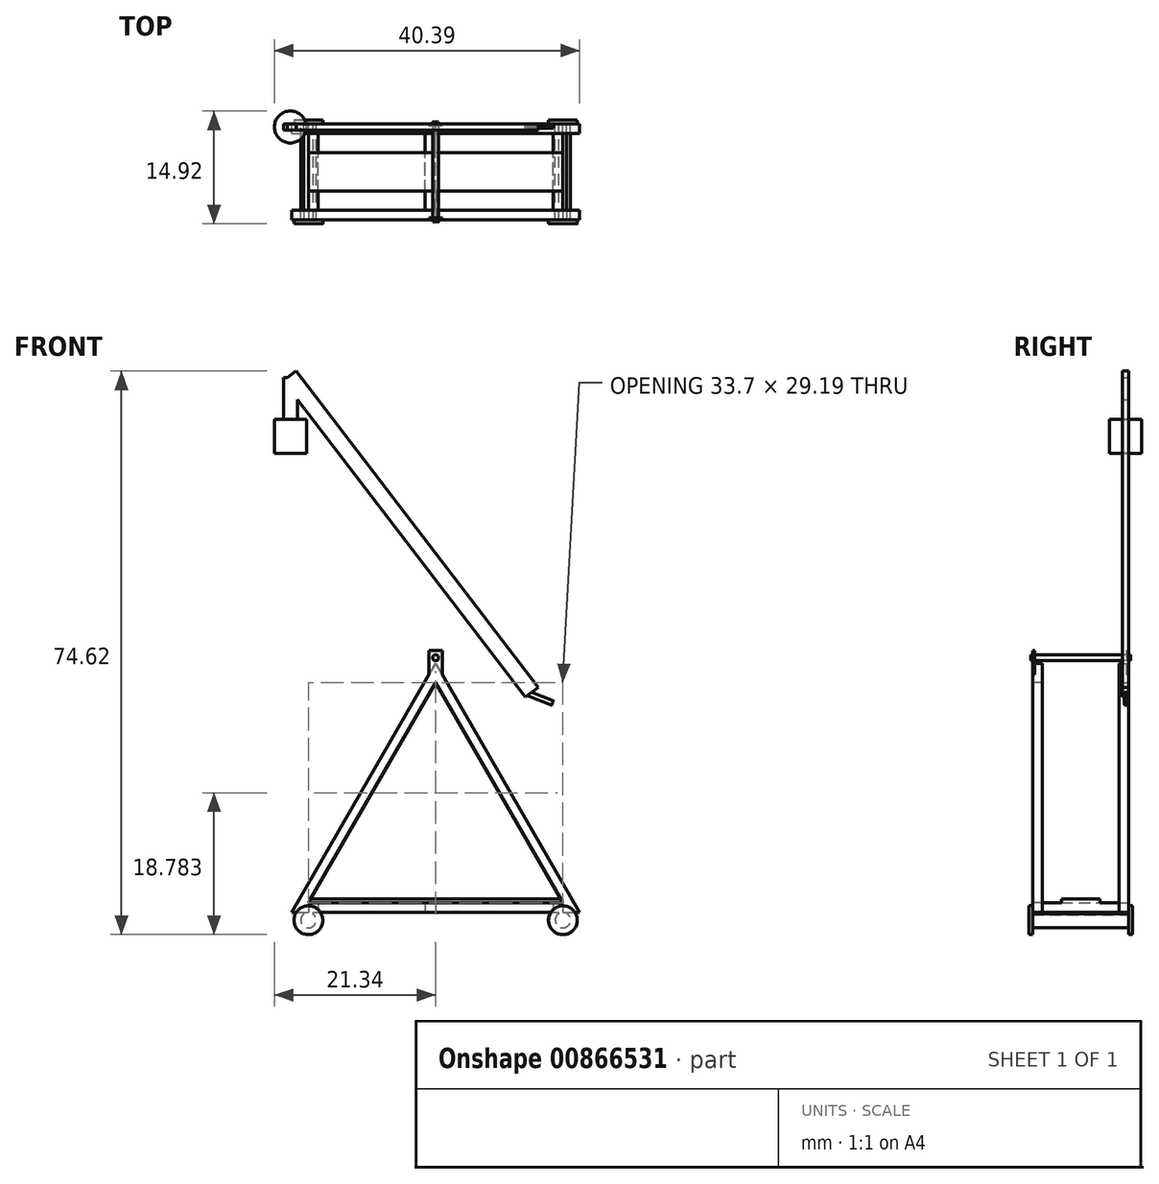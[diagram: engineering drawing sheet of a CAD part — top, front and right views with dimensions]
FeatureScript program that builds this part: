
annotation { "Feature Type Name" : "Feature", "Feature Type Description" : "" }
export const myFeature = defineFeature(function(context is Context, id is Id, definition is map)
    precondition{}
    {
        {
            var Q0;
            Q0=qCreatedBy(makeId("Front.planeOp"),FACE);
            var sketch = newSketch(context, id + "F0", { "sketchPlane" : qUnion([Q0])});
            skLineSegment(sketch, "E0", {"start": v(0, 0) * mm, "end": v(38.1, 0) * mm});
            skLineSegment(sketch, "E1", {"start": v(0, 0) * mm, "end": v(19.05, 33) * mm});
            skLineSegment(sketch, "E2", {"start": v(19.05, 33) * mm, "end": v(38.1, 0) * mm});
            skLineSegment(sketch, "E3.0", {"start": v(2.2, 1.27) * mm, "end": v(19.05, 30.46) * mm});
            skLineSegment(sketch, "E3.1", {"start": v(2.2, 1.27) * mm, "end": v(35.9, 1.27) * mm});
            skLineSegment(sketch, "E3.2", {"start": v(19.05, 30.46) * mm, "end": v(35.9, 1.27) * mm});
            skCircle(sketch, "E4", {"center": v(2.2, -1.02) * mm, "radius": 1.02 * mm});
            skCircle(sketch, "E5", {"center": v(35.9, -1.02) * mm, "radius": 1.02 * mm});
            skLineSegment(sketch, "E6", {"start": v(36.41, -0.14) * mm, "end": v(36.41, 0) * mm});
            skLineSegment(sketch, "E7", {"start": v(1.61, -0.19) * mm, "end": v(1.61, 0) * mm});
            skLineSegment(sketch, "E8", {"start": v(2.88, -0.26) * mm, "end": v(2.88, 0) * mm});
            skLineSegment(sketch, "E9", {"start": v(35.36, -0.16) * mm, "end": v(35.36, 0) * mm});
            skSolve(sketch);
        }
        {
            var Q0;
            Q0=makeQuery(id+"F0.imprint","IMPRINT",FACE,{"disambiguationData":[TD([[makeQuery(id+"F0.imprint","IMPRINT",EDGE,{"derivedFrom":sQuery(id+"F0.wireOp",EDGE,"E0")}),1.0]])]});
            extrude(context, id + "F1", {"entities" : qUnion([Q0]), "depth" : 1.27 * mm, "offsetDistance" : 25.4 * mm});
        }
        {
            var Q0;
            Q0=makeQuery(id+"F1.opExtrude","CAP_FACE",FACE,{"disambiguationData":[OSD([sQuery(id+"F0.wireOp",EDGE,"E0"),sQuery(id+"F0.wireOp",EDGE,"E1"),sQuery(id+"F0.wireOp",EDGE,"E2"),sQuery(id+"F0.wireOp",EDGE,"E3.0"),sQuery(id+"F0.wireOp",EDGE,"E3.1"),sQuery(id+"F0.wireOp",EDGE,"E3.2")])],"isStart":false});
            var sketch = newSketch(context, id + "F2", { "sketchPlane" : qUnion([Q0])});
            skLineSegment(sketch, "E10.bottom", {"start": v(2.2, 1.27) * mm, "end": v(3.47, 1.27) * mm});
            skLineSegment(sketch, "E10.top", {"start": v(2.2, 0) * mm, "end": v(3.47, 0) * mm});
            skLineSegment(sketch, "E10.left", {"start": v(2.2, 1.27) * mm, "end": v(2.2, 0) * mm});
            skLineSegment(sketch, "E10.right", {"start": v(3.47, 1.27) * mm, "end": v(3.47, 0) * mm});
            skLineSegment(sketch, "E11.bottom", {"start": v(17.67, 1.27) * mm, "end": v(19.05, 1.27) * mm});
            skLineSegment(sketch, "E11.top", {"start": v(17.67, 0) * mm, "end": v(19.05, 0) * mm});
            skLineSegment(sketch, "E11.left", {"start": v(17.67, 1.27) * mm, "end": v(17.67, 0) * mm});
            skLineSegment(sketch, "E11.right", {"start": v(19.05, 1.27) * mm, "end": v(19.05, 0) * mm});
            skLineSegment(sketch, "E12.bottom", {"start": v(35.9, 1.27) * mm, "end": v(34.62, 1.27) * mm});
            skLineSegment(sketch, "E12.top", {"start": v(35.9, 0) * mm, "end": v(34.62, 0) * mm});
            skLineSegment(sketch, "E12.left", {"start": v(35.9, 1.27) * mm, "end": v(35.9, 0) * mm});
            skLineSegment(sketch, "E12.right", {"start": v(34.62, 1.27) * mm, "end": v(34.62, 0) * mm});
            skSolve(sketch);
        }
        {
            var Q0;
            Q0=makeQuery(id+"F2.imprint","IMPRINT",FACE,{"disambiguationData":[TD([[makeQuery(id+"F2.imprint","IMPRINT",EDGE,{"derivedFrom":sQuery(id+"F2.wireOp",EDGE,"E10.bottom")}),-1.0]])]});
            var Q1;
            Q1=makeQuery(id+"F2.imprint","IMPRINT",FACE,{"disambiguationData":[TD([[makeQuery(id+"F2.imprint","IMPRINT",EDGE,{"derivedFrom":sQuery(id+"F2.wireOp",EDGE,"E11.bottom")}),-1.0]])]});
            var Q2;
            Q2=makeQuery(id+"F2.imprint","IMPRINT",FACE,{"disambiguationData":[TD([[makeQuery(id+"F2.imprint","IMPRINT",EDGE,{"derivedFrom":sQuery(id+"F2.wireOp",EDGE,"E12.bottom")}),-1.0]])]});
            extrude(context, id + "F3", {"entities" : qUnion([Q0, Q1, Q2]), "operationType" : NewBodyOperationType.ADD, "depth" : 5.08 * mm, "offsetDistance" : 25.4 * mm});
        }
        {
            var Q0;
            Q0=makeQuery(id+"F0.imprint","IMPRINT",FACE,{"disambiguationData":[TD([[makeQuery(id+"F0.imprint","IMPRINT",EDGE,{"derivedFrom":sQuery(id+"F0.wireOp",EDGE,"E4")}),1.0]])]});
            var Q1;
            Q1=makeQuery(id+"F0.imprint","IMPRINT",FACE,{"disambiguationData":[TD([[makeQuery(id+"F0.imprint","IMPRINT",EDGE,{"derivedFrom":sQuery(id+"F0.wireOp",EDGE,"E5")}),1.0]])]});
            var Q2;
            {var subQ0=sQuery(id+"F0.wireOp",EDGE,"E7");Q2=makeQuery(id+"F0.imprint","IMPRINT",FACE,{"disambiguationData":[TD([[makeQuery(id+"F0.imprint","IMPRINT",EDGE,{"derivedFrom":subQ0}),-1.0]])]});}
            var Q3;
            {var subQ0=sQuery(id+"F0.wireOp",EDGE,"E6");Q3=makeQuery(id+"F0.imprint","IMPRINT",FACE,{"disambiguationData":[TD([[makeQuery(id+"F0.imprint","IMPRINT",EDGE,{"derivedFrom":subQ0}),1.0]])]});}
            var Q4;
            {var subQ0=sQuery(id+"F0.wireOp",EDGE,"E9");Q4=makeQuery(id+"F0.imprint","IMPRINT",FACE,{"disambiguationData":[TD([[makeQuery(id+"F0.imprint","IMPRINT",EDGE,{"derivedFrom":subQ0}),-1.0]])]});}
            var Q5;
            {var subQ0=sQuery(id+"F0.wireOp",EDGE,"E8");Q5=makeQuery(id+"F0.imprint","IMPRINT",FACE,{"disambiguationData":[TD([[makeQuery(id+"F0.imprint","IMPRINT",EDGE,{"derivedFrom":subQ0}),1.0]])]});}
            extrude(context, id + "F4", {"entities" : qUnion([Q0, Q1, Q2, Q3, Q4, Q5]), "operationType" : NewBodyOperationType.ADD, "depth" : 6.35 * mm, "offsetDistance" : 25.4 * mm});
        }
        {
            var Q0;
            {var subQ0=sQuery(id+"F0.wireOp",EDGE,"E0");Q0=makeQuery(id+"F4.boolean.opBoolean","MERGE",FACE,{"derivedFrom":[makeQuery(id+"F1.opExtrude","CAP_FACE",FACE,{"disambiguationData":[OSD([subQ0,sQuery(id+"F0.wireOp",EDGE,"E1"),sQuery(id+"F0.wireOp",EDGE,"E2"),sQuery(id+"F0.wireOp",EDGE,"E3.0"),sQuery(id+"F0.wireOp",EDGE,"E3.1"),sQuery(id+"F0.wireOp",EDGE,"E3.2")])],"isStart":true}),makeQuery(id+"F4.opExtrude","CAP_FACE",FACE,{"disambiguationData":[OSD([subQ0,sQuery(id+"F0.wireOp",EDGE,"E4"),sQuery(id+"F0.wireOp",EDGE,"E7"),sQuery(id+"F0.wireOp",EDGE,"E8")])],"isStart":true}),makeQuery(id+"F4.opExtrude","CAP_FACE",FACE,{"disambiguationData":[OSD([subQ0,sQuery(id+"F0.wireOp",EDGE,"E5"),sQuery(id+"F0.wireOp",EDGE,"E6"),sQuery(id+"F0.wireOp",EDGE,"E9")])],"isStart":true})]});}
            var sketch = newSketch(context, id + "F5", { "sketchPlane" : qUnion([Q0])});
            skCircle(sketch, "E13", {"center": v(-35.9, -1.02) * mm, "radius": 1.9 * mm});
            skCircle(sketch, "E14", {"center": v(-2.2, -1.02) * mm, "radius": 1.9 * mm});
            skSolve(sketch);
        }
        {
            var Q0;
            {var subQ2=sQuery(id+"F0.wireOp",EDGE,"E5");Q0=makeQuery(id+"F5.imprint","IMPRINT",FACE,{"disambiguationData":[TD([[makeQuery(id+"F5.imprint","IMPRINT",EDGE,{"derivedFrom":makeQuery(id+"F4.opExtrude","CAP_EDGE",EDGE,{"disambiguationData":[OSD([subQ2])],"isStart":true})}),1.0]])]});}
            var Q1;
            {var subQ14=sQuery(id+"F0.wireOp",EDGE,"E5");Q1=makeQuery(id+"F5.imprint","IMPRINT",FACE,{"disambiguationData":[TD([[makeQuery(id+"F5.imprint","IMPRINT",EDGE,{"derivedFrom":makeQuery(id+"F4.opExtrude","CAP_EDGE",EDGE,{"disambiguationData":[OSD([subQ14])],"isStart":true})}),-1.0]])]});}
            var Q2;
            {var subQ10=sQuery(id+"F0.wireOp",EDGE,"E4");Q2=makeQuery(id+"F5.imprint","IMPRINT",FACE,{"disambiguationData":[TD([[makeQuery(id+"F5.imprint","IMPRINT",EDGE,{"derivedFrom":makeQuery(id+"F4.opExtrude","CAP_EDGE",EDGE,{"disambiguationData":[OSD([subQ10])],"isStart":true})}),-1.0]])]});}
            var Q3;
            {var subQ2=sQuery(id+"F0.wireOp",EDGE,"E4");Q3=makeQuery(id+"F5.imprint","IMPRINT",FACE,{"disambiguationData":[TD([[makeQuery(id+"F5.imprint","IMPRINT",EDGE,{"derivedFrom":makeQuery(id+"F4.opExtrude","CAP_EDGE",EDGE,{"disambiguationData":[OSD([subQ2])],"isStart":true})}),1.0]])]});}
            extrude(context, id + "F6", {"entities" : qUnion([Q0, Q1, Q2, Q3]), "operationType" : NewBodyOperationType.ADD, "depth" : 0.5 * mm, "offsetDistance" : 25.4 * mm});
        }
        {
            var Q0;
            Q0=makeQuery(id+"F3.boolean.opBoolean","MERGE",FACE,{"derivedFrom":[makeQuery(id+"F1.opExtrude","SWEPT_FACE",FACE,{"disambiguationData":[OSD([sQuery(id+"F0.wireOp",EDGE,"E3.1")])]}),makeQuery(id+"F3.opExtrude","SWEPT_FACE",FACE,{"disambiguationData":[OSD([sQuery(id+"F2.wireOp",EDGE,"E10.bottom")])]}),makeQuery(id+"F3.opExtrude","SWEPT_FACE",FACE,{"disambiguationData":[OSD([sQuery(id+"F2.wireOp",EDGE,"E11.bottom")])]}),makeQuery(id+"F3.opExtrude","SWEPT_FACE",FACE,{"disambiguationData":[OSD([sQuery(id+"F2.wireOp",EDGE,"E12.bottom")])]})]});
            var sketch = newSketch(context, id + "F7", { "sketchPlane" : qUnion([Q0])});
            skLineSegment(sketch, "E15.bottom", {"start": v(35.9, -3.81) * mm, "end": v(2.2, -3.81) * mm});
            skLineSegment(sketch, "E15.top", {"start": v(35.9, -6.35) * mm, "end": v(2.2, -6.35) * mm});
            skLineSegment(sketch, "E15.left", {"start": v(35.9, -3.81) * mm, "end": v(35.9, -6.35) * mm});
            skLineSegment(sketch, "E15.right", {"start": v(2.2, -3.81) * mm, "end": v(2.2, -6.35) * mm});
            skSolve(sketch);
        }
        {
            var Q0;
            {var subQ0=sQuery(id+"F7.wireOp",EDGE,"E15.bottom");var subQ1=sQuery(id+"F0.wireOp",EDGE,"E3.1");var subQ2=makeQuery(id+"F3.opExtrude","SWEPT_EDGE",EDGE,{"disambiguationData":[OSD([subQ1,sQuery(id+"F2.wireOp",EDGE,"E11.bottom"),sQuery(id+"F2.wireOp",EDGE,"E11.left")])]});var subQ3=makeQuery(id+"F7.imprint","INTERSECT",VERTEX,{"derivedFrom":[subQ2,subQ0]});Q0=makeQuery(id+"F7.imprint","IMPRINT",FACE,{"disambiguationData":[TD([[makeQuery(id+"F7.imprint","IMPRINT",EDGE,{"disambiguationData":[TD([[subQ3,-1.0]])],"derivedFrom":subQ0}),1.0]])]});}
            var Q1;
            {var subQ0=sQuery(id+"F7.wireOp",EDGE,"E15.right");Q1=makeQuery(id+"F7.imprint","IMPRINT",FACE,{"disambiguationData":[TD([[makeQuery(id+"F7.imprint","IMPRINT",EDGE,{"derivedFrom":subQ0}),-1.0]])]});}
            var Q2;
            {var subQ0=sQuery(id+"F7.wireOp",EDGE,"E15.bottom");var subQ1=sQuery(id+"F2.wireOp",EDGE,"E11.bottom");var subQ2=sQuery(id+"F0.wireOp",EDGE,"E3.1");var subQ3=makeQuery(id+"F3.opExtrude","SWEPT_EDGE",EDGE,{"disambiguationData":[OSD([subQ2,subQ1,sQuery(id+"F2.wireOp",EDGE,"E11.right")])]});var subQ4=makeQuery(id+"F7.imprint","INTERSECT",VERTEX,{"derivedFrom":[subQ3,subQ0]});Q2=makeQuery(id+"F7.imprint","IMPRINT",FACE,{"disambiguationData":[TD([[makeQuery(id+"F7.imprint","IMPRINT",EDGE,{"disambiguationData":[TD([[subQ4,-1.0]])],"derivedFrom":subQ0}),1.0]])]});}
            var Q3;
            {var subQ0=sQuery(id+"F7.wireOp",EDGE,"E15.bottom");var subQ1=sQuery(id+"F0.wireOp",EDGE,"E3.1");var subQ2=makeQuery(id+"F3.opExtrude","SWEPT_EDGE",EDGE,{"disambiguationData":[OSD([subQ1,sQuery(id+"F2.wireOp",EDGE,"E12.bottom"),sQuery(id+"F2.wireOp",EDGE,"E12.right")])]});var subQ3=makeQuery(id+"F7.imprint","INTERSECT",VERTEX,{"derivedFrom":[subQ2,subQ0]});Q3=makeQuery(id+"F7.imprint","IMPRINT",FACE,{"disambiguationData":[TD([[makeQuery(id+"F7.imprint","IMPRINT",EDGE,{"disambiguationData":[TD([[subQ3,-1.0]])],"derivedFrom":subQ0}),1.0]])]});}
            var Q4;
            {var subQ0=sQuery(id+"F7.wireOp",EDGE,"E15.left");Q4=makeQuery(id+"F7.imprint","IMPRINT",FACE,{"disambiguationData":[TD([[makeQuery(id+"F7.imprint","IMPRINT",EDGE,{"derivedFrom":subQ0}),1.0]])]});}
            extrude(context, id + "F8", {"entities" : qUnion([Q0, Q1, Q2, Q3, Q4]), "operationType" : NewBodyOperationType.ADD, "depth" : 0.5 * mm, "offsetDistance" : 25.4 * mm});
        }
        {
            var Q0;
            {var subQ0=sQuery(id+"F0.wireOp",EDGE,"E0");Q0=makeQuery(id+"F4.boolean.opBoolean","MERGE",FACE,{"derivedFrom":[makeQuery(id+"F1.opExtrude","CAP_FACE",FACE,{"disambiguationData":[OSD([subQ0,sQuery(id+"F0.wireOp",EDGE,"E1"),sQuery(id+"F0.wireOp",EDGE,"E2"),sQuery(id+"F0.wireOp",EDGE,"E3.0"),sQuery(id+"F0.wireOp",EDGE,"E3.1"),sQuery(id+"F0.wireOp",EDGE,"E3.2")])],"isStart":true}),makeQuery(id+"F4.opExtrude","CAP_FACE",FACE,{"disambiguationData":[OSD([subQ0,sQuery(id+"F0.wireOp",EDGE,"E4"),sQuery(id+"F0.wireOp",EDGE,"E7"),sQuery(id+"F0.wireOp",EDGE,"E8")])],"isStart":true}),makeQuery(id+"F4.opExtrude","CAP_FACE",FACE,{"disambiguationData":[OSD([subQ0,sQuery(id+"F0.wireOp",EDGE,"E5"),sQuery(id+"F0.wireOp",EDGE,"E6"),sQuery(id+"F0.wireOp",EDGE,"E9")])],"isStart":true})]});}
            var sketch = newSketch(context, id + "F9", { "sketchPlane" : qUnion([Q0])});
            skLineSegment(sketch, "E16", {"start": v(-19.91, 31.5) * mm, "end": v(-18.19, 31.5) * mm});
            skLineSegment(sketch, "E17", {"start": v(-18.19, 31.5) * mm, "end": v(-18.19, 34.66) * mm});
            skLineSegment(sketch, "E18", {"start": v(-18.19, 34.66) * mm, "end": v(-19.91, 34.66) * mm});
            skLineSegment(sketch, "E19", {"start": v(-19.91, 34.66) * mm, "end": v(-19.91, 31.5) * mm});
            skCircle(sketch, "E20", {"center": v(-19.05, 33.74) * mm, "radius": 0.4 * mm});
            skSolve(sketch);
        }
        {
            var Q0;
            {var subQ4=sQuery(id+"F9.wireOp",EDGE,"E17");Q0=makeQuery(id+"F9.imprint","IMPRINT",FACE,{"disambiguationData":[TD([[makeQuery(id+"F9.imprint","IMPRINT",EDGE,{"derivedFrom":subQ4}),1.0]])]});}
            var Q1;
            {var subQ0=sQuery(id+"F9.wireOp",EDGE,"E16");Q1=makeQuery(id+"F9.imprint","IMPRINT",FACE,{"disambiguationData":[TD([[makeQuery(id+"F9.imprint","IMPRINT",EDGE,{"derivedFrom":subQ0}),1.0]])]});}
            extrude(context, id + "F10", {"entities" : qUnion([Q0, Q1]), "operationType" : NewBodyOperationType.ADD, "oppositeDirection" : true, "depth" : 0.25 * mm, "offsetDistance" : 25.4 * mm});
        }
        {
            var Q0;
            Q0=makeQuery(id+"F9.imprint","IMPRINT",FACE,{"disambiguationData":[TD([[makeQuery(id+"F9.imprint","IMPRINT",EDGE,{"derivedFrom":sQuery(id+"F9.wireOp",EDGE,"E20")}),1.0]])]});
            extrude(context, id + "F11", {"entities" : qUnion([Q0]), "operationType" : NewBodyOperationType.ADD, "depth" : 0.25 * mm, "offsetDistance" : 25.4 * mm, "hasSecondDirection" : true, "secondDirectionOppositeDirection" : true, "secondDirectionDepth" : 6.35 * mm});
        }
        {
            var Q0;
            Q0=makeQuery(id+"F1.opExtrude","SWEPT_BODY",BODY,{"disambiguationData":[OSD([sQuery(id+"F0.wireOp",EDGE,"E0"),sQuery(id+"F0.wireOp",EDGE,"E1"),sQuery(id+"F0.wireOp",EDGE,"E2"),sQuery(id+"F0.wireOp",EDGE,"E3.0"),sQuery(id+"F0.wireOp",EDGE,"E3.1"),sQuery(id+"F0.wireOp",EDGE,"E3.2")])]});
            var Q1;
            {var subQ0=sQuery(id+"F0.wireOp",EDGE,"E0");Q1=makeQuery(id+"F8.boolean.opBoolean","MERGE",FACE,{"derivedFrom":[makeQuery(id+"F3.opExtrude","CAP_FACE",FACE,{"disambiguationData":[OSD([sQuery(id+"F2.wireOp",EDGE,"E11.bottom"),sQuery(id+"F2.wireOp",EDGE,"E11.top"),sQuery(id+"F2.wireOp",EDGE,"E11.left"),sQuery(id+"F2.wireOp",EDGE,"E11.right")])],"isStart":false}),makeQuery(id+"F4.boolean.opBoolean","MERGE",FACE,{"derivedFrom":[makeQuery(id+"F3.opExtrude","CAP_FACE",FACE,{"disambiguationData":[OSD([sQuery(id+"F2.wireOp",EDGE,"E10.bottom"),sQuery(id+"F2.wireOp",EDGE,"E10.top"),sQuery(id+"F2.wireOp",EDGE,"E10.left"),sQuery(id+"F2.wireOp",EDGE,"E10.right")])],"isStart":false}),makeQuery(id+"F4.opExtrude","CAP_FACE",FACE,{"disambiguationData":[OSD([subQ0,sQuery(id+"F0.wireOp",EDGE,"E4"),sQuery(id+"F0.wireOp",EDGE,"E7"),sQuery(id+"F0.wireOp",EDGE,"E8")])],"isStart":false})]}),makeQuery(id+"F4.boolean.opBoolean","MERGE",FACE,{"derivedFrom":[makeQuery(id+"F3.opExtrude","CAP_FACE",FACE,{"disambiguationData":[OSD([sQuery(id+"F2.wireOp",EDGE,"E12.bottom"),sQuery(id+"F2.wireOp",EDGE,"E12.top"),sQuery(id+"F2.wireOp",EDGE,"E12.left"),sQuery(id+"F2.wireOp",EDGE,"E12.right")])],"isStart":false}),makeQuery(id+"F4.opExtrude","CAP_FACE",FACE,{"disambiguationData":[OSD([subQ0,sQuery(id+"F0.wireOp",EDGE,"E5"),sQuery(id+"F0.wireOp",EDGE,"E6"),sQuery(id+"F0.wireOp",EDGE,"E9")])],"isStart":false})]}),makeQuery(id+"F8.opExtrude","SWEPT_FACE",FACE,{"disambiguationData":[OSD([sQuery(id+"F7.wireOp",EDGE,"E15.top")])]})]});}
            mirror(context, id + "F12", {"operationType" : NewBodyOperationType.ADD, "entities" : qUnion([Q0]), "mirrorPlane" : qUnion([Q1])});
        }
        {
            var Q0;
            Q0=qCreatedBy(makeId("Front.planeOp"),FACE);
            var sketch = newSketch(context, id + "F13", { "sketchPlane" : qUnion([Q0])});
            skLineSegment(sketch, "E21.bottom", {"start": v(1.68, 70.21) * mm, "end": v(32.61, 29.84) * mm});
            skLineSegment(sketch, "E21.top", {"start": v(0, 68.92) * mm, "end": v(30.93, 28.55) * mm});
            skLineSegment(sketch, "E21.left", {"start": v(1.68, 70.21) * mm, "end": v(0, 68.92) * mm});
            skLineSegment(sketch, "E21.right", {"start": v(32.61, 29.84) * mm, "end": v(30.93, 28.55) * mm});
            skLineSegment(sketch, "E22.bottom", {"start": v(0.76, 67.94) * mm, "end": v(-1.11, 67.94) * mm});
            skLineSegment(sketch, "E22.top", {"start": v(0.76, 60.81) * mm, "end": v(-1.11, 60.81) * mm});
            skLineSegment(sketch, "E22.left", {"start": v(0.76, 67.94) * mm, "end": v(0.76, 60.81) * mm});
            skLineSegment(sketch, "E22.right", {"start": v(-1.11, 67.94) * mm, "end": v(-1.11, 60.81) * mm});
            skLineSegment(sketch, "E23", {"start": v(1.68, 70.21) * mm, "end": v(0.54, 71.7) * mm});
            skLineSegment(sketch, "E24", {"start": v(0.54, 71.7) * mm, "end": v(-1.46, 70.16) * mm});
            skLineSegment(sketch, "E25", {"start": v(0, 68.92) * mm, "end": v(-1.14, 70.41) * mm});
            skLineSegment(sketch, "E26", {"start": v(-1.11, 67.94) * mm, "end": v(-1.11, 70.85) * mm});
            skLineSegment(sketch, "E27", {"start": v(-1.11, 70.85) * mm, "end": v(0.76, 70.85) * mm});
            skSolve(sketch);
        }
        {
            var Q0;
            Q0=makeQuery(id+"F13.imprint","IMPRINT",FACE,{"disambiguationData":[TD([[makeQuery(id+"F13.imprint","IMPRINT",EDGE,{"derivedFrom":sQuery(id+"F13.wireOp",EDGE,"E21.bottom")}),-1.0]])]});
            var Q1;
            {var subQ5=sQuery(id+"F13.wireOp",EDGE,"E21.left");Q1=makeQuery(id+"F13.imprint","IMPRINT",FACE,{"disambiguationData":[TD([[makeQuery(id+"F13.imprint","IMPRINT",EDGE,{"derivedFrom":subQ5}),-1.0]])]});}
            var Q2;
            {var subQ3=sQuery(id+"F13.wireOp",EDGE,"E22.bottom");Q2=makeQuery(id+"F13.imprint","IMPRINT",FACE,{"disambiguationData":[TD([[makeQuery(id+"F13.imprint","IMPRINT",EDGE,{"derivedFrom":subQ3}),-1.0]])]});}
            var Q3;
            Q3=makeQuery(id+"F13.imprint","IMPRINT",FACE,{"disambiguationData":[TD([[makeQuery(id+"F13.imprint","IMPRINT",EDGE,{"derivedFrom":sQuery(id+"F13.wireOp",EDGE,"E22.bottom")}),1.0]])]});
            var Q4;
            {var subQ0=sQuery(id+"F13.wireOp",EDGE,"E27");var subQ1=sQuery(id+"F13.wireOp",EDGE,"E24");var subQ2=makeQuery(id+"F13.imprint","INTERSECT",VERTEX,{"derivedFrom":[subQ1,subQ0]});Q4=makeQuery(id+"F13.imprint","IMPRINT",FACE,{"disambiguationData":[TD([[makeQuery(id+"F13.imprint","IMPRINT",EDGE,{"disambiguationData":[TD([[subQ2,-1.0]])],"derivedFrom":subQ1}),-1.0]])]});}
            extrude(context, id + "F14", {"entities" : qUnion([Q0, Q1, Q2, Q3, Q4]), "depth" : 0.8 * mm, "offsetDistance" : 25 * mm});
        }
        {
            var Q0;
            Q0=makeQuery(id+"F14.opExtrude","SWEPT_FACE",FACE,{"disambiguationData":[OSD([sQuery(id+"F13.wireOp",EDGE,"E22.top")])]});
            var sketch = newSketch(context, id + "F15", { "sketchPlane" : qUnion([Q0])});
            skLineSegment(sketch, "E28", {"start": v(-0.18, 0) * mm, "end": v(-0.18, 0.8) * mm});
            skCircle(sketch, "E29", {"center": v(-0.18, 0.4) * mm, "radius": 2.11 * mm});
            skSolve(sketch);
        }
        {
            var Q0;
            Q0=makeQuery(id+"F15.imprint","IMPRINT",FACE,{"disambiguationData":[TD([[makeQuery(id+"F15.imprint","IMPRINT",EDGE,{"derivedFrom":sQuery(id+"F15.wireOp",EDGE,"E29")}),1.0]])]});
            extrude(context, id + "F16", {"entities" : qUnion([Q0]), "operationType" : NewBodyOperationType.ADD, "oppositeDirection" : true, "depth" : 4.5 * mm, "offsetDistance" : 25 * mm});
        }
        {
            var Q0;
            Q0=makeQuery(id+"F14.opExtrude","CAP_FACE",FACE,{"disambiguationData":[OSD([sQuery(id+"F13.wireOp",EDGE,"E21.bottom"),sQuery(id+"F13.wireOp",EDGE,"E21.top"),sQuery(id+"F13.wireOp",EDGE,"E21.right"),sQuery(id+"F13.wireOp",EDGE,"E22.top"),sQuery(id+"F13.wireOp",EDGE,"E22.left"),sQuery(id+"F13.wireOp",EDGE,"E22.right"),sQuery(id+"F13.wireOp",EDGE,"E23"),sQuery(id+"F13.wireOp",EDGE,"E24"),sQuery(id+"F13.wireOp",EDGE,"E26"),sQuery(id+"F13.wireOp",EDGE,"E27")])],"isStart":true});
            var sketch = newSketch(context, id + "F17", { "sketchPlane" : qUnion([Q0])});
            skLineSegment(sketch, "E30", {"start": v(-31.77, 29.2) * mm, "end": v(-34.65, 28.05) * mm});
            skLineSegment(sketch, "E31", {"start": v(-34.65, 28.05) * mm, "end": v(-34.4, 27.43) * mm});
            skLineSegment(sketch, "E32", {"start": v(-34.4, 27.43) * mm, "end": v(-31.15, 28.72) * mm});
            skSolve(sketch);
        }
        {
            var Q0;
            {var subQ0=sQuery(id+"F17.wireOp",EDGE,"E30");Q0=makeQuery(id+"F17.imprint","IMPRINT",FACE,{"disambiguationData":[TD([[makeQuery(id+"F17.imprint","IMPRINT",EDGE,{"derivedFrom":subQ0}),1.0]])]});}
            extrude(context, id + "F18", {"entities" : qUnion([Q0]), "operationType" : NewBodyOperationType.ADD, "oppositeDirection" : true, "depth" : 0.56 * mm, "offsetDistance" : 25 * mm, "hasSecondDirection" : true, "secondDirectionOppositeDirection" : true, "secondDirectionDepth" : 0.2 * mm});
        }
        {
            var Q0;
            Q0=makeQuery(id+"F18.opExtrude","CAP_EDGE",EDGE,{"disambiguationData":[OSD([sQuery(id+"F17.wireOp",EDGE,"E30")])],"isStart":true});
            var Q1;
            Q1=makeQuery(id+"F18.opExtrude","CAP_EDGE",EDGE,{"disambiguationData":[OSD([sQuery(id+"F17.wireOp",EDGE,"E30")])],"isStart":false});
            var Q2;
            Q2=makeQuery(id+"F18.opExtrude","CAP_EDGE",EDGE,{"disambiguationData":[OSD([sQuery(id+"F17.wireOp",EDGE,"E32")])],"isStart":true});
            var Q3;
            Q3=makeQuery(id+"F18.opExtrude","CAP_EDGE",EDGE,{"disambiguationData":[OSD([sQuery(id+"F17.wireOp",EDGE,"E32")])],"isStart":false});
            fillet(context, id + "F19", {"entities" : qUnion([Q0, Q1, Q2, Q3]), "radius" : 0.2 * mm, "tangentPropagation" : true, "allowEdgeOverflow" : false});
        }
    });
